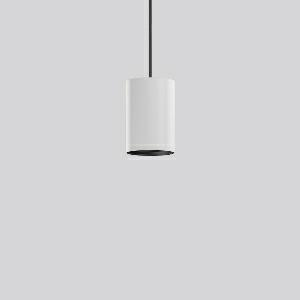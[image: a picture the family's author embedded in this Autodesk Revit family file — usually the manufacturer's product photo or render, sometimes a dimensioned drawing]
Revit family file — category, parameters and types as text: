
# Revit family: deecos_p_maxi_911540_002_2_5e54
name_source: partatom
category: Lighting Fixtures
units: mm (PartAtom-declared; Revit-internal decimal feet)

## family parameters
Cut with Voids When Loaded = No
Host = Face
Light Source = No
Part Type = Normal
Room Calculation Point = No
Round Connector Dimension = Use Diameter
Shared = No

## types (1)
- DEECOS P maxi (1 x LED Modul 927, 3500 lm, 2700)
    Apparent Load = 35 VA
    Approval mark = CE
    CIE Flux Codes = 97 100 100 100 100
    Color Rendering = 92
    Color Temperature = 2700
    Default Elevation = 1800 mm
    Description = Series: DEECOS P maxi
Cylindrical pendant luminaire. Housing: die-cast aluminium, powder-coated. Canopy made of powder-coated sheet steel with magnetic attachment. Optical assembly with lens made of plastic (polycarbonate) for the best homogeneous light distribution - can be changed without tools. Best colour rendering index Ra>90. Transparent suspension cable 2 m, can be shortened. High quality converter without flickering and stroboscopic effect. The following accessories can be mounted without use of tools: interchangeable lenses, honeycomb louvre, clear and frosted diffusers, white interchangeable plastic ring. Decorative recessed suspension set available as accessory. 
Colour: traffic white, matt (RAL 9016)
Diameter: 123 mm
Height: 181 mm
Suspension length: 2000 mm
Lamp: LED
Socket: without socket
Colour temperature: 2700K
Colour rendering index (CRI): 92
System power: 35 W
Rated luminous flux: 3500 lm
Luminous efficiency: 100 lm/W
Control gear: Regulated power supply
Protection class: I
Type of protection: IP 20
    Height = 181 mm
    Lamp = 1 x LED Modul 927
    Lamp Light Flux = 3500 lm
    Lamp count = 1
    Length = 123 mm
    Lifetime = 50000 h
    Luminous efficacy = 100 lm/W
    Manufacturer = RZB
    ModVariant = No
    Model = 911540.002.2
    Mounting Place = Ceiling
    Mounting Type = Pendant
    Number of Poles = 1
    OnlyDefault = Yes
    Power Factor = 1
    Product Name = DEECOS P maxi
    Product group = Pendant luminaires
    ProductGroupID = 902
    Protection Class = Protection class I
    Protection Degree = IP 20
    RLX_Detail_Level = 1
    RLX_Emergency_Light_Flux = 0 lm
    RLX_Emergency_Type = 0
    RLX_Emergency_Type_DB = No
    RlxData = <blob elided: 35609 chars, md5=97f7ea9f>
    Socket = socket
    Standby Power = 0 W
    System Light Flux = 3500 lm
    System Power = 35 W
    Type Comments = Product without accessories
    Type Image = 911480.002.jpg
    URL = http://relux.com
    VarID = ---
    Voltage = 230 V
    Voltage Range = 220-240 V
    Weight = 0.00 kg
    Width = 0 mm  [stored 0 ft]

note: [stored X ft] marks values corroborated as IEEE doubles in the binary element streams (Revit-internal decimal feet)

## geometry (parser evidence)
native form markers: Blend x4, Sweep x8
no freeform markers — native parametric forms only
